# Revit family: 04120373
name_source: partatom
category: Plumbing Fixtures
revit_build: Autodesk Revit 2018 (Build: 20170223_1515(x64)
units: mm (PartAtom-declared; Revit-internal decimal feet)

## family parameters
Always vertical = Yes
Cut with Voids When Loaded = No
OmniClass Number = 23.45.55.00
OmniClass Title = Sanitary Faucets, Wastes
Part Type = Normal
Room Calculation Point = No
Round Connector Dimension = Use Diameter
Shared = No
Work Plane-Based = No

## types (1)
- 04120373 Shower hose, L=1750
    2D/3D/BIM Files URL = http://static.hansa.com
    3D View = https://static.hansa.com
    AssetType = Fixed
    BIMObjectName = 04120373
    BodyMaterial = Brass
    Brand = HANSA
    Catalog Drawing URL = http://static.hansa.com
    Category = Health & Care
    CloseOffRating = 0
    Color = Chrome
    Connection Size = G1/2
    DurationUnit = Year
    EAN Number = 4015474255043
    EN Standard = EN 1113
    ETIM Class Number = EC011535 Shower hose
    FDV Document URL = http://www.hansa.com
    FaucetMainMaterial = Brass
    Finish = Polished
    FlowCoefficient = 0
    Group = Shower hose
    IfcExportAs = IfcValveType
    IfcExportType = FAUCET
    InletConnectionSize = 10 mm  [stored 0.0328084 ft]
    Interactive AR View URL = https://static.hansa.com
    Length Height = 1750 mm
    Manufacturer = HANSA
    ManufacturerName = HANSA
    ManufacturerURL = http://www.hansa.com
    Market = International;Germany;Austria;Switzerland;Belgium;Netherlands;France;Czech Republic;Slovakia;Italy;Spain
    Material = Brass
    Mobile Product Information URL = http://mpi.hansa.com
    Model = 04120373 Shower hose, L=1750
    ModelReference = 04120373
    NBSDescription = Shower mixers
    NBSReference = 45-35-70/335
    Name = 04120373 Shower hose, L=1750
    Name_en = 04120373 Shower hose, L=1750
    NominalDepth = 23 mm
    NominalHeight = 169 mm  [stored 0.554462 ft]
    NominalWidth = 23 mm
    Product Code = 04120373
    Product Family = HANSAMEDIPRO
    Product Image URL = http://static.hansa.com
    Product URL = http://static.hansa.com
    Revision = 4
    Sales Package dimensions (LxWxH) = 350 x 250 x 20
    Shape = Sculptured
    Shower Parts = Twist guard for shower hose
    Size = G1/2, L=1750 mm
    Surface treatment = Chrome
    Technical DataSheet URL = http://www.hansa.com
    UNSPSC Class Number = 30181800 Faucet and shower heads, jets and parts and accessories
    URL Declaration of Conformity = http://static.hansa.com
    URL REACH = http://static.hansa.com
    Uniclass2 = Pr_40_30_96_78
    Uniclass2015Description = Shower manual water supply sets
    Uniclass2015Reference = Pr_40_20_87_78
    Version = 4
    VersionDate = 01/07/2022
    Warranty Information URL = http://warranty.hansa.com
    WarrantyDescription = http://warranty.hansa.com
    WarrantyDurationUnit = Year

note: [stored X ft] marks values corroborated as IEEE doubles in the binary element streams (Revit-internal decimal feet)

## geometry (parser evidence)
native form markers: Sweep x3
no freeform markers — native parametric forms only
